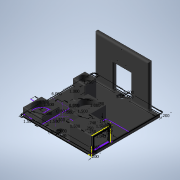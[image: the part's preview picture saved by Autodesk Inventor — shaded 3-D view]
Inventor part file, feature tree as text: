
AUTODESK INVENTOR PART (.ipt)
format: ipt  version: 2020 (Build 240168000, 168)  size: 1,741,824 bytes
history: native  units: in
note: dims shown in document units (in); Inventor stores cm internally (conversion verified against a paired STEP export)
features: extrude x15, sketch x9, fillet x7, hole x2
ambient origin geometry x8: Origin, YZ Plane, XZ Plane, XY Plane, X Axis, Y Axis, Z Axis, Center Point
bodies: Solid1 (feature_tree)
feature tree (33):
  sketch  "Sketch1"  dims[d0=5.6in d1=6.0in]
  extrude  "Extrusion1"  Depth=6.0in
  hole  "Hole1"  [1 undecoded]
  extrude  "Extrusion2"  Depth=5.6in
  extrude  "Extrusion3"  Depth=5.6in
  extrude  "Extrusion4"  Depth=0.25in TaperAngle=0.0deg
  extrude  "Extrusion5"  Depth=1.5in
  extrude  "Extrusion6"  Depth=1.5in
  hole  "Hole2"  [1 undecoded]
  extrude  "Extrusion7"  TaperAngle=180.0deg  [1 undecoded]
  extrude  "Extrusion8"  Depth=1.5in
  extrude  "Extrusion9"  Depth=1.5in
  sketch  "Sketch6"  dims[d11=0.266in d12=0.75in d13=0.625in d14=0.19in d15=0.5635in d16=1.0in d17=0.8108in d18=1.5in]
  extrude  "Extrusion10"  Depth=1.5in
  sketch  "Sketch7"  dims[d19=0.6in d20=1.5in]
  extrude  "Extrusion11"  Depth=1.5in
  extrude  "Extrusion12"  Depth=1.3in
  extrude  "Extrusion13"  Depth=1.3in
  fillet  "Fillet1"  Radius=0.5in
  fillet  "Fillet2"  Radius=0.5in
  fillet  "Fillet3"  Radius=1.0in
  fillet  "Fillet4"  Radius=1.5in
  fillet  "Fillet5"  Radius=0.325in
  fillet  "Fillet6"  Radius=2.0in
  fillet  "Fillet7"  Radius=1.5in
  sketch  "Sketch8"  dims[d21=1.5in d22=0.6in]
  sketch  "Sketch9"  dims[d23=1.5in d24=180.0deg d25=1.5in d26=1.5in d27=1.5in d28=1.5in d29=1.3in d30=1.3in d31=0.5in d32=0.0in d33=0.5in d34=0.0in d35=1.0in d36=0.0in d37=1.5in d38=0.325in d39=2.0in d40=0.0in d41=1.5in d42=0.0in d43=0.333in d44=0.96in d45=0.356in d46=0.356in d47=0.134in d48=0.75in d49=0.256in d50=0.118in d51=90.0deg d52=1.0in d53=0.8108in d54=1.75in d55=1.0in d56=1.0in d57=1.0in d58=0.78in d59=1.5in d60=0.0in d61=0.25in d62=0.25in d63=1.5in d64=0.0in d65=1.25in d66=0.0in d67=0.125in d68=0.125in d69=0.125in d70=0.125in d71=1.725in d72=0.0in d73=0.25in d74=0.25in d75=1.043in d76=0.748in d77=0.25in d78=0.0in d79=0.25in d80=0.25in d81=0.0625in d82=0.0625in d83=0.0625in d84=0.0625in d85=0.1875in d86=0.0in d87=0.125in d88=0.0in d89=0.125in d90=0.125in d91=0.0625in d92=0.0625in d93=0.0625in d94=0.0625in d95=0.0625in d96=0.0197in d97=0.0in d98=0.0197in d99=0.0in]
  extrude  "Extrusion14"  Depth=0.333in
  extrude  "Extrusion15"  Depth=0.96in
  sketch  "Sketch2"  dims[d2=0.5in d3=90.0deg]
  sketch  "Sketch3"  dims[d4=0.5in d5=5.6in]
  sketch  "Sketch4"  dims[d6=0.2in d7=5.6in]
  sketch  "Sketch5"  dims[d8=0.2in d9=0.25in d10=0.0in]
note: 3 required parameter values undecoded (feature->parameter linkage not recoverable at this tier; creation-order binding heuristic only, values carry confidence <= 0.55)
